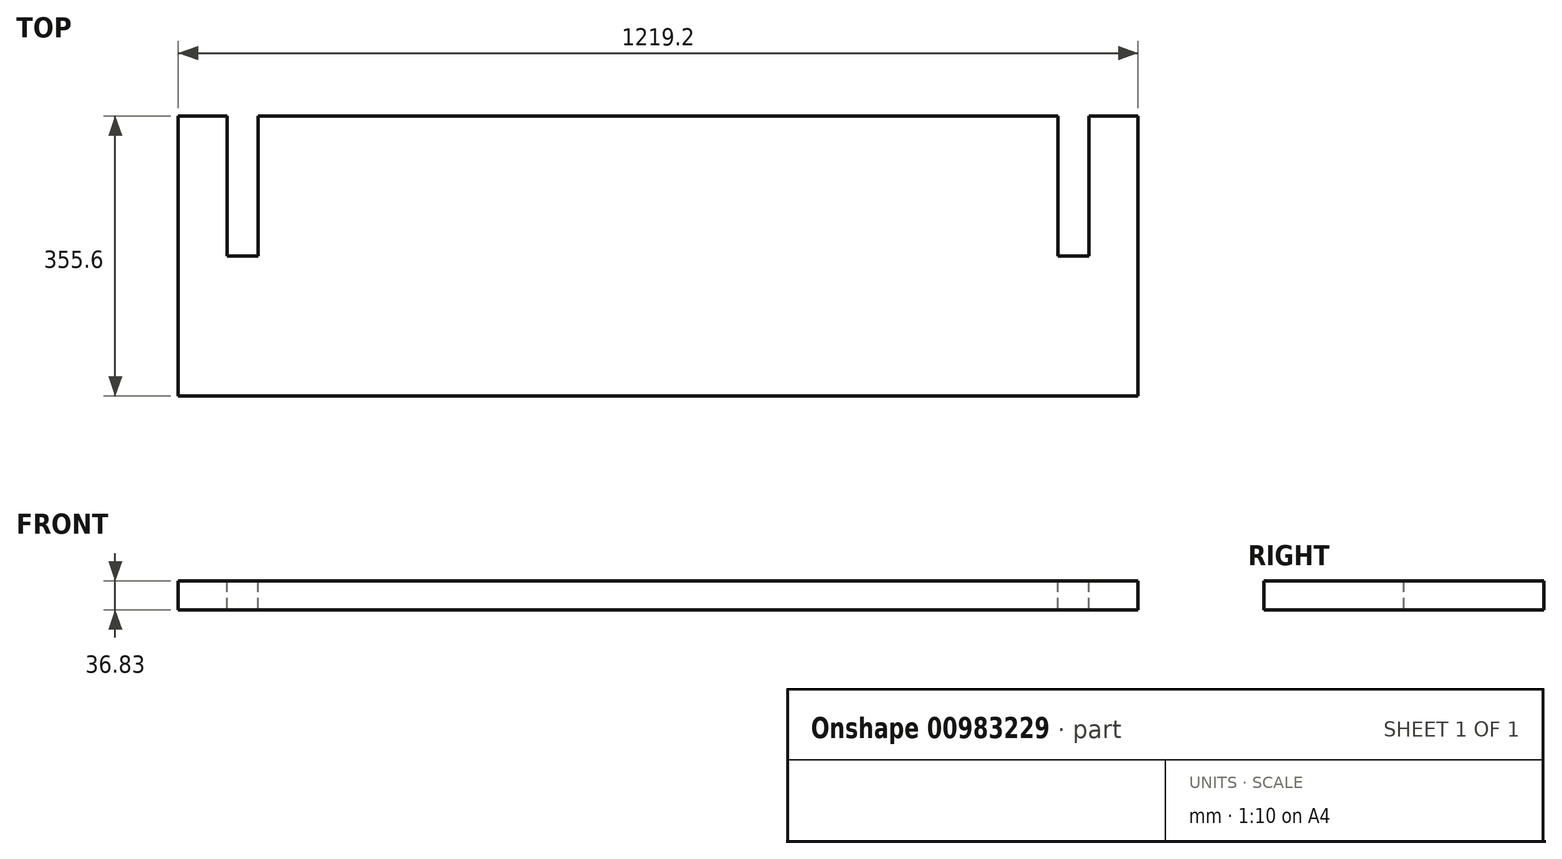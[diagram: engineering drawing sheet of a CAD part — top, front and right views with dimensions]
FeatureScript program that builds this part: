
annotation { "Feature Type Name" : "Feature", "Feature Type Description" : "" }
export const myFeature = defineFeature(function(context is Context, id is Id, definition is map)
    precondition{}
    {
        {
            var Q0;
            Q0=qCreatedBy(makeId("Top.planeOp"),FACE);
            var sketch = newSketch(context, id + "F0", { "sketchPlane" : qUnion([Q0])});
            skLineSegment(sketch, "E0.bottom", {"start": v(609.6, -177.8) * mm, "end": v(-609.6, -177.8) * mm});
            skLineSegment(sketch, "E0.top", {"start": v(609.6, 177.8) * mm, "end": v(-609.6, 177.8) * mm});
            skLineSegment(sketch, "E0.left", {"start": v(609.6, -177.8) * mm, "end": v(609.6, 177.8) * mm});
            skLineSegment(sketch, "E0.right", {"start": v(-609.6, -177.8) * mm, "end": v(-609.6, 177.8) * mm});
            skPoint(sketch, "E0.middle", {"position": v(0, 0) * mm});
            skSolve(sketch);
        }
        {
            var Q0;
            Q0=makeQuery(id+"F0.imprint","IMPRINT",FACE,{"disambiguationData":[TD([[makeQuery(id+"F0.imprint","IMPRINT",EDGE,{"derivedFrom":sQuery(id+"F0.wireOp",EDGE,"E0.bottom")}),-1.0]])]});
            extrude(context, id + "F1", {"entities" : qUnion([Q0]), "depth" : 36.83 * mm, "offsetDistance" : 25.4 * mm});
        }
        {
            var Q0;
            Q0=makeQuery(id+"F1.opExtrude","CAP_FACE",FACE,{"disambiguationData":[OSD([sQuery(id+"F0.wireOp",EDGE,"E0.bottom"),sQuery(id+"F0.wireOp",EDGE,"E0.top"),sQuery(id+"F0.wireOp",EDGE,"E0.left"),sQuery(id+"F0.wireOp",EDGE,"E0.right")])],"isStart":false});
            var sketch = newSketch(context, id + "F2", { "sketchPlane" : qUnion([Q0])});
            skLineSegment(sketch, "E1.bottom", {"start": v(-547.37, 177.8) * mm, "end": v(-508, 177.8) * mm});
            skLineSegment(sketch, "E1.top", {"start": v(-547.37, 0) * mm, "end": v(-508, 0) * mm});
            skLineSegment(sketch, "E1.left", {"start": v(-547.37, 177.8) * mm, "end": v(-547.37, 0) * mm});
            skLineSegment(sketch, "E1.right", {"start": v(-508, 177.8) * mm, "end": v(-508, 0) * mm});
            skLineSegment(sketch, "E2.MirrorCS", {"start": v(547.37, 0) * mm, "end": v(508, 0) * mm});
            skLineSegment(sketch, "E3.MirrorCS", {"start": v(508, 177.8) * mm, "end": v(508, 0) * mm});
            skLineSegment(sketch, "E4.MirrorCS", {"start": v(547.37, 177.8) * mm, "end": v(508, 177.8) * mm});
            skLineSegment(sketch, "E5.MirrorCS", {"start": v(547.37, 177.8) * mm, "end": v(547.37, 0) * mm});
            skSolve(sketch);
        }
        {
            var Q0;
            Q0=qSketchRegion(id+"F2",true);
            extrude(context, id + "F3", {"entities" : qUnion([Q0]), "operationType" : NewBodyOperationType.REMOVE, "endBound" : BoundingType.UP_TO_NEXT, "oppositeDirection" : true, "depth" : 25.4 * mm, "offsetDistance" : 25.4 * mm});
        }
    });
